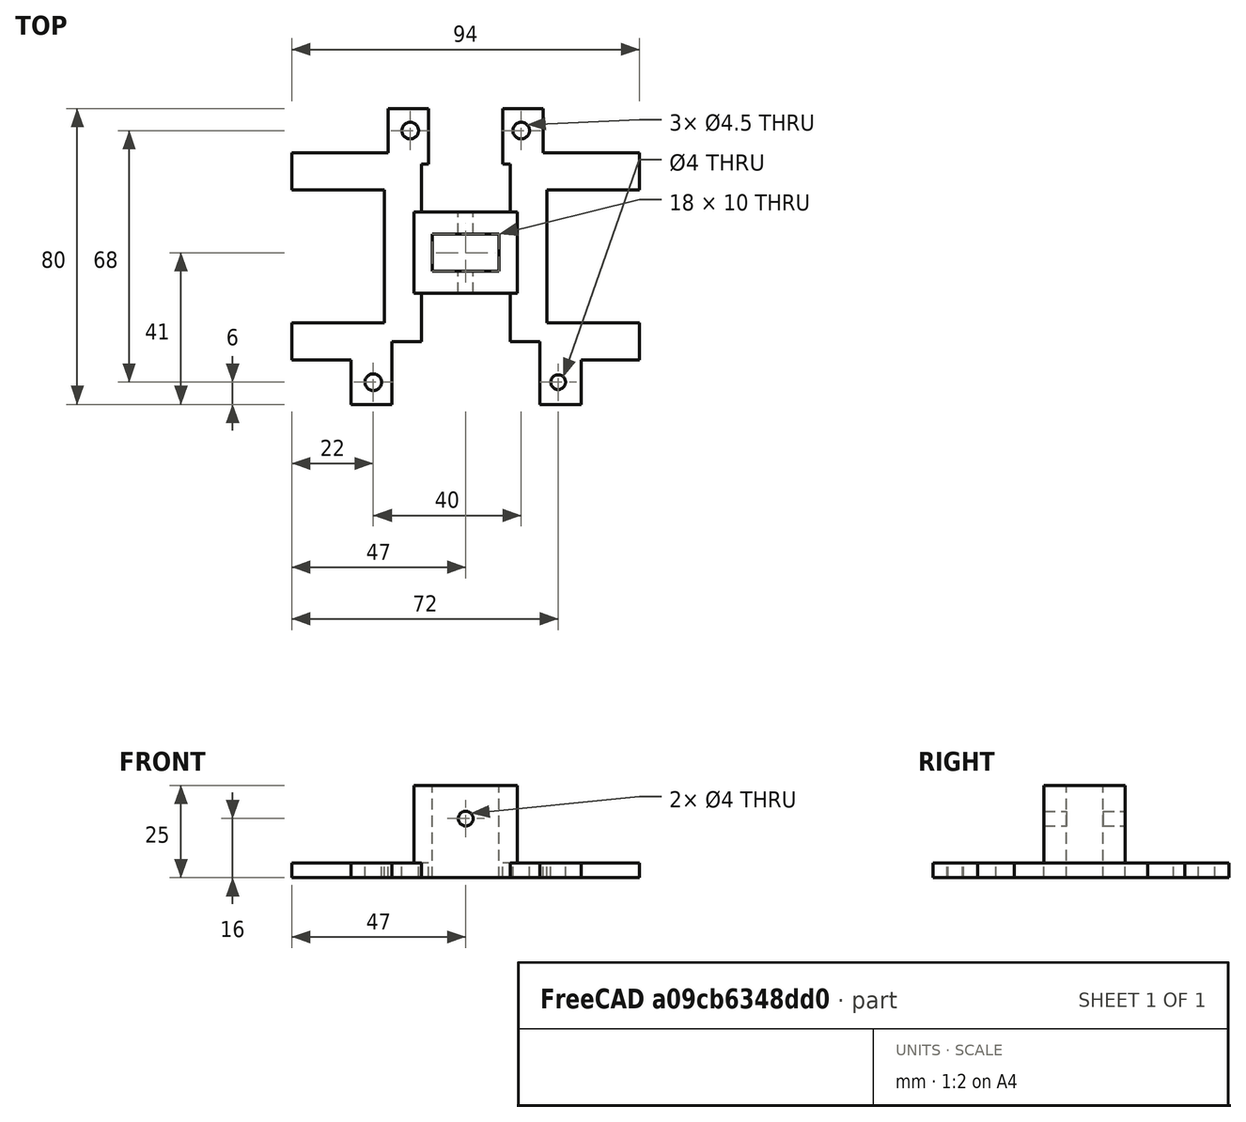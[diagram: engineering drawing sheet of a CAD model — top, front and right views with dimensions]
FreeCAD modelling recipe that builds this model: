
FCSTD DOCUMENT  (FreeCAD 0.19R24267 +148 (Git))
Label: spine04132022
License: All rights reserved
LicenseURL: http://en.wikipedia.org/wiki/All_rights_reserved
objects: Part::Box×13, Part::Cylinder×6, Part::MultiFuse×5, Part::Cut×4
note: 28 computed .brp shape members not serialized (recipe doc carries the construction recipe); baked Part::Feature solids carry a one-line shape summary decoded from their .brp

FEATURE [Part::Cylinder] Cylinder103  label="Cylinder107"
  Angle = 360
  AttacherType = Attacher::AttachEngine3D
  Height = 10
  Placement = pos=(62,3,0) rot=(0,0,1;0rad)
  Radius = 2.25
FEATURE [Part::Box] Box064  label="base005"
  AttacherType = Attacher::AttachEngine3D
  Height = 4
  Length = 26
  Placement = pos=(-10.25,68,0) rot=(0,0,1;0rad)
  Width = 12
FEATURE [Part::Box] Box060  label="base001"
  AttacherType = Attacher::AttachEngine3D
  Height = 4
  Length = 94
  Width = 80
FEATURE [Part::Box] Box061  label="base002"
  AttacherType = Attacher::AttachEngine3D
  Height = 4
  Length = 26
  Width = 12
FEATURE [Part::Box] Box062  label="base003"
  AttacherType = Attacher::AttachEngine3D
  Height = 4
  Length = 26
  Placement = pos=(68,0,0) rot=(0,0,1;0rad)
  Width = 12
FEATURE [Part::Cylinder] Cylinder104  label="Cylinder103"
  Angle = 360
  AttacherType = Attacher::AttachEngine3D
  Height = 10
  Placement = pos=(72,71,0) rot=(0,0,1;0rad)
  Radius = 2.25
FEATURE [Part::Cylinder] Cylinder106  label="Cylinder104"
  Angle = 360
  AttacherType = Attacher::AttachEngine3D
  Height = 10
  Placement = pos=(22,71,0) rot=(0,0,1;0rad)
  Radius = 2
FEATURE [Part::Cylinder] Cylinder105  label="Cylinder108"
  Angle = 360
  AttacherType = Attacher::AttachEngine3D
  Height = 10
  Placement = pos=(32,3,0) rot=(0,0,1;0rad)
  Radius = 2.25
FEATURE [Part::Box] Box081  label="Cube039"
  AttacherType = Attacher::AttachEngine3D
  Height = 10
  Length = 25
  Placement = pos=(82,26,140) rot=(0,0,1;0rad)
  Width = 36
FEATURE [Part::Box] Box082  label="Cube040"
  AttacherType = Attacher::AttachEngine3D
  Height = 10
  Length = 40
  Placement = pos=(40,4,140) rot=(0,0,1;0rad)
  Width = 17
FEATURE [Part::Box] Box073  label="baseSpineCut"
  AttacherType = Attacher::AttachEngine3D
  Height = 25
  Length = 18
  Placement = pos=(51,40,140) rot=(0,0,1;0rad)
  Width = 10
FEATURE [Part::Cylinder] Cylinder107  label="Cylinder109"
  Angle = 360
  AttacherType = Attacher::AttachEngine3D
  Height = 10
  Radius = 1
FEATURE [Part::MultiFuse] Fusion123  label="screwIns001"
  Placement = pos=(0,3,0) rot=(0,0,1;0rad)
  Shapes = -> [Cylinder105,Cylinder107,Cylinder103,Cylinder104,Cylinder106]
FEATURE [Part::Box] Box080  label="Cube038"
  AttacherType = Attacher::AttachEngine3D
  Height = 10
  Length = 25
  Placement = pos=(13,26,140) rot=(0,0,1;0rad)
  Width = 36
FEATURE [Part::Box] Box063  label="base004"
  AttacherType = Attacher::AttachEngine3D
  Height = 4
  Length = 26
  Placement = pos=(78,68,0) rot=(0,0,1;0rad)
  Width = 12
FEATURE [Part::MultiFuse] Fusion122
  Shapes = -> [Box064,Box063,Box061,Box062]
FEATURE [Part::Cut] Cut019  label="baseNew"
  Base = -> Box060
  Tool = -> Fusion122
FEATURE [Part::Cut] Cut020  label="baseNew001"
  Base = -> Cut019
  Placement = pos=(107,84,140) rot=(0,0,1;3.14159rad)
  Tool = -> Fusion123
FEATURE [Part::Box] Box083  label="Cube041"
  AttacherType = Attacher::AttachEngine3D
  Height = 10
  Length = 24
  Placement = pos=(48,21,140) rot=(0,0,1;0rad)
  Width = 13
FEATURE [Part::Box] Box084  label="Cube042"
  AttacherType = Attacher::AttachEngine3D
  Height = 10
  Length = 24
  Placement = pos=(48,56,140) rot=(0,0,1;0rad)
  Width = 13
FEATURE [Part::Box] Box085  label="Cube043"
  AttacherType = Attacher::AttachEngine3D
  Height = 10
  Length = 15
  Placement = pos=(70,69,140) rot=(0,0,1;1.5708rad)
  Width = 20
FEATURE [Part::MultiFuse] Fusion133  label="baseCuts"
  Shapes = -> [Box085,Box083,Box082,Box081,Box084,Box080]
FEATURE [Part::Box] Box086  label="baseSpineIn"
  AttacherType = Attacher::AttachEngine3D
  Height = 25
  Length = 28
  Placement = pos=(46,34,140) rot=(0,0,1;0rad)
  Width = 22
FEATURE [Part::MultiFuse] Fusion  label="base"
  Shapes = -> [Cut020,Box086]
FEATURE [Part::MultiFuse] Fusion134  label="baseCuts001"
  Shapes = -> [Box073,Fusion133]
FEATURE [Part::Cut] Cut
  Base = -> Fusion
  Tool = -> Fusion134
FEATURE [Part::Cylinder] Cylinder
  Angle = 360
  AttacherType = Attacher::AttachEngine3D
  Height = 50
  Placement = pos=(60,17,156) rot=(-1,0,0;1.5708rad)
  Radius = 2
FEATURE [Part::Cut] Cut021  label="spine"
  Base = -> Cut
  Tool = -> Cylinder
